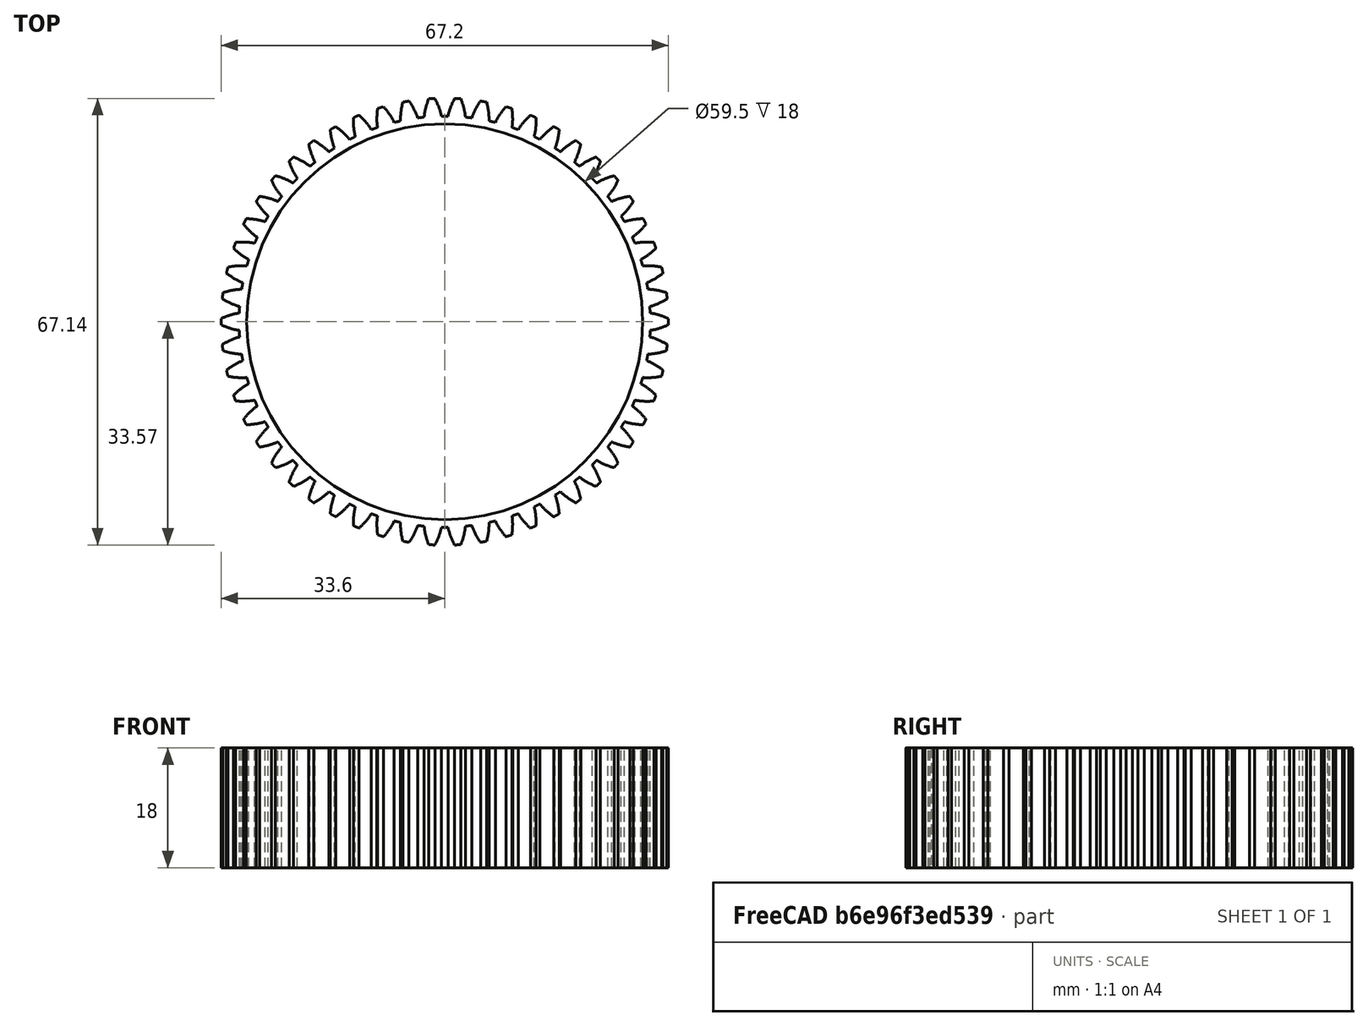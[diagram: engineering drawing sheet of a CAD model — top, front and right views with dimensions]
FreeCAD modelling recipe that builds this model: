
FCSTD DOCUMENT  (FreeCAD 0.21R33771 (Git))
Label: DD_002a_FlexTeeth_2
License: All rights reserved
LicenseURL: http://en.wikipedia.org/wiki/All_rights_reserved
objects: PartDesign::FeatureBase×1, Sketcher::SketchObject×1, PartDesign::Pocket×1, PartDesign::Body×1
note: 5 computed .brp shape members not serialized (recipe doc carries the construction recipe); baked Part::Feature solids carry a one-line shape summary decoded from their .brp

FEATURE [PartDesign::FeatureBase] BaseFeature
FEATURE [Sketcher::SketchObject] Sketch
  FullyConstrained = true
  MapMode = 5
  Placement = pos=(0,0,0) rot=(1,0,0;3.14159rad)
  sketch-geometry (1):
    g0: Circle CenterX=0 CenterY=0 CenterZ=0 NormalX=0 NormalY=0 NormalZ=1 AngleXU=0 Radius=29.75
  constraints (2):
    c: Coincident(g0,g-1)
    c: Diameter(g0) = 59.5
FEATURE [PartDesign::Pocket] Pocket
  BaseFeature = -> BaseFeature
  Direction = (0,0,1)
  Length = 5
  Length2 = 5
  Profile = -> Sketch
  ReferenceAxis = -> Sketch [N_Axis]
  Type = 1
FEATURE [PartDesign::Body] Body
  Group = -> [BaseFeature,Sketch,Pocket]
  Origin = -> Origin
  Tip = -> Pocket
